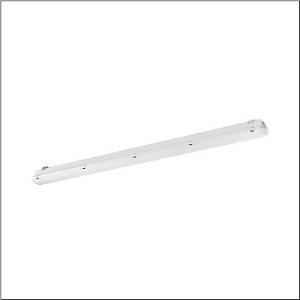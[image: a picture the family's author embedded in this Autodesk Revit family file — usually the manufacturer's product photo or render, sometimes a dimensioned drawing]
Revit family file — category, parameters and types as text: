
# Revit family: monsun_r__11xtreme_mo_51fe10mp480s_c233
name_source: partatom
category: Lighting Fixtures
units: mm (PartAtom-declared; Revit-internal decimal feet)

## family parameters
Cut with Voids When Loaded = No
Host = Face
Light Source = No
Part Type = Normal
Room Calculation Point = No
Round Connector Dimension = Use Diameter
Shared = No

## types (1)
- --- (1 x LED, 8000 lm, 40.1 W, 4000K)
    Apparent Load = 40 VA
    CIE Flux Codes = 47 77 93 94 100
    Color Rendering = 80
    Color Temperature = 4000K
    Default Elevation = 1800 mm
    Description = Monsun® 11Xtreme MO, damp-proof luminaire, chain hanger, primary optical cover: enclosure, of PMMA, light emission: direct distribution, primary light characteristic: symmetric, installation type: suspended mounting, surface-mounted, horizontal mounting, vertical mounting, LED, rated luminous flux: 8.000lm, luminous efficacy: 200lm/W, light colour: 840, colour temperature: 4000K, control gear: ON/OFF Multilumen, with terminal, 3-pole, max. 2.5mm², mains connection: 220..240V, AC, 50/60Hz, rated input power: 40W, luminaire housing, of glass-fibre reinforced polyester, uncoated, bright grey, incl. chain hanger, length: 1.590mm, width: 90mm, height: 88mm, clip for enclosure, of stainless steel (V2A), ceiling mounting element, of stainless steel (V2A), chain hanger, of stainless steel (V2A), protection rating (complete): IP66, insulation class (complete): insulation class I (protective earthing), certification: CE, ENEC, VDE, UKCA, protection symbol: D, impact resistance: IK04, permissible operating ambient temperature: -35..+55°C (at 8000lm) / 60°C (at 4100lm), standard: EN 50419, EN 60598-2-1, contact your sales advisor before using the luminaires in applications with unclear chemical exposure, large temperature fluctuations or condensation-forming humidity, LABS conformity tested according to VDMA 24364:2018-05, no direct snow, no direct sun, no direct rain, for indoor or canopied outdoor use, corresponds to IFS (International Featured Standards) requirements for safety and quality in the food industry, packaging unit: 1 piece
    Height = 88 mm
    Lamp = 1 x LED
    Lamp Light Flux = 8000 lm
    Lamp Power = 40.1 W
    Lamp count = 1
    Length = 1590 mm
    Luminous efficacy = 200 lm/W
    Manufacturer = Siteco
    ModVariant = No
    Model = 51FE10MP480S
    Mounting Place = Ceiling
    Mounting Type = Surface mounted
    Number of Poles = 1
    OnlyDefault = Yes
    Power Factor = 1
    Product Name = Monsun® 11Xtreme MO
    Product group = damp-proof luminaire
    ProductGroupID = 300
    Protection Class = Protection class I
    Protection Degree = IP 66
    RLX_Detail_Level = 1
    RLX_Emergency_Light_Flux = 0 lm
    RLX_Emergency_Type = 0
    RLX_Emergency_Type_DB = No
    RlxData = <blob elided: 85317 chars, md5=e40062c4>
    Socket = socket
    Standby Power = 0 W
    System Light Flux = 8000 lm
    System Power = 40 W
    Type Comments = factory setting: luminous flux: 100 % | (A | C | E) | 95 mA
    Type Image = l_1349234.jpg
    URL = http://relux.com
    VarID = @adj_018610
    Voltage = 0 V
    Weight = 0.00 kg
    Width = 90 mm

## geometry (parser evidence)
native form markers: Blend x4, Sweep x13
no freeform markers — native parametric forms only
